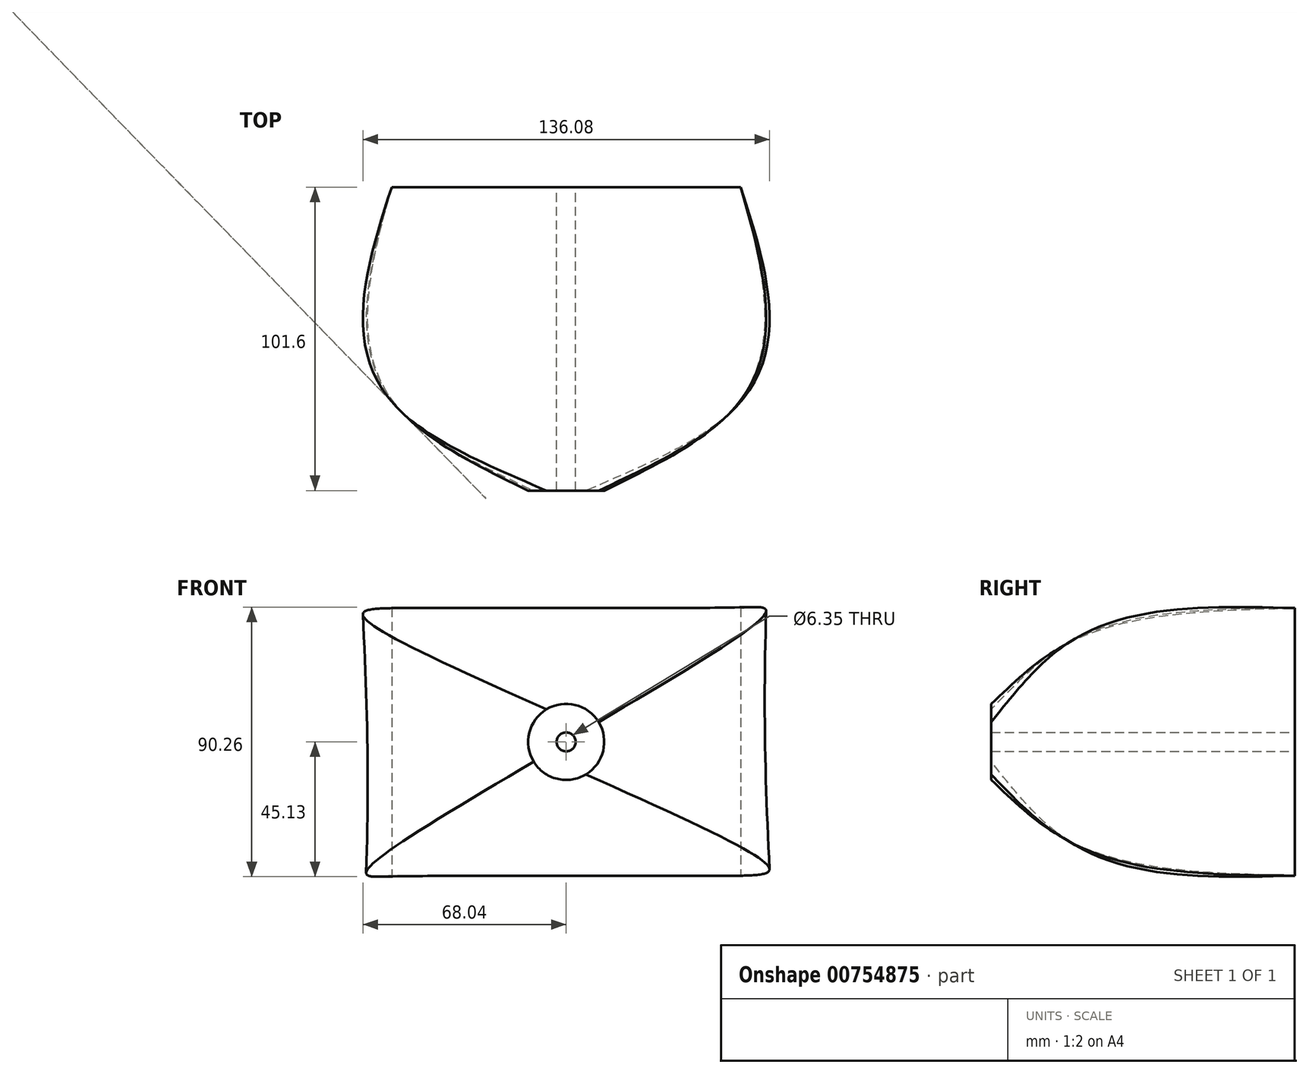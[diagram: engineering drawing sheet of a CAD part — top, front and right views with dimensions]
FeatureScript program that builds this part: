
annotation { "Feature Type Name" : "Feature", "Feature Type Description" : "" }
export const myFeature = defineFeature(function(context is Context, id is Id, definition is map)
    precondition{}
    {
        {
            var Q0;
            Q0=qCreatedBy(makeId("Front.planeOp"),FACE);
            var sketch = newSketch(context, id + "F0", { "sketchPlane" : qUnion([Q0])});
            skLineSegment(sketch, "E0.bottom", {"start": v(58.39, 44.79) * mm, "end": v(-58.39, 44.79) * mm});
            skLineSegment(sketch, "E0.top", {"start": v(58.39, -44.79) * mm, "end": v(-58.39, -44.79) * mm});
            skLineSegment(sketch, "E0.left", {"start": v(58.39, 44.79) * mm, "end": v(58.39, -44.79) * mm});
            skLineSegment(sketch, "E0.right", {"start": v(-58.39, 44.79) * mm, "end": v(-58.39, -44.79) * mm});
            skPoint(sketch, "E0.middle", {"position": v(0, 0) * mm});
            skSolve(sketch);
        }
        {
            var Q0;
            Q0=qCreatedBy(makeId("Front.planeOp"),FACE);
            cPlane(context, id + "F1", {"entities" : qUnion([Q0]), "cplaneType" : CPlaneType.OFFSET, "offset" : 76.2 * mm, "width" : 152.4 * mm, "height" : 152.4 * mm});
        }
        {
            var Q0;
            Q0=qCreatedBy(id+"F1.planeOp",FACE);
            var sketch = newSketch(context, id + "F2", { "sketchPlane" : qUnion([Q0])});
            skLineSegment(sketch, "E1.bottom", {"start": v(54.14, 32.93) * mm, "end": v(-54.14, 32.93) * mm});
            skLineSegment(sketch, "E1.top", {"start": v(54.14, -32.93) * mm, "end": v(-54.14, -32.93) * mm});
            skLineSegment(sketch, "E1.left", {"start": v(54.14, 32.93) * mm, "end": v(54.14, -32.93) * mm});
            skLineSegment(sketch, "E1.right", {"start": v(-54.14, 32.93) * mm, "end": v(-54.14, -32.93) * mm});
            skPoint(sketch, "E1.middle", {"position": v(0, 0) * mm});
            skSolve(sketch);
        }
        {
            var Q0;
            Q0=makeQuery(id+"F0.imprint","IMPRINT",FACE,{"disambiguationData":[TD([[makeQuery(id+"F0.imprint","IMPRINT",EDGE,{"derivedFrom":sQuery(id+"F0.wireOp",EDGE,"E0.bottom")}),1.0]])]});
            cPlane(context, id + "F3", {"entities" : qUnion([Q0]), "cplaneType" : CPlaneType.OFFSET, "offset" : 101.6 * mm, "width" : 152.4 * mm, "height" : 152.4 * mm});
        }
        {
            var Q0;
            Q0=qCreatedBy(id+"F3.planeOp",FACE);
            var sketch = newSketch(context, id + "F4", { "sketchPlane" : qUnion([Q0])});
            skCircle(sketch, "E2", {"center": v(0, 0) * mm, "radius": 12.73 * mm});
            skSolve(sketch);
        }
        {
            var Q0;
            Q0 = qSketchRegion(id + "F0", true);
            var Q1;
            Q1 = qSketchRegion(id + "F2", true);
            var Q2;
            Q2 = qSketchRegion(id + "F4", true);
            loft(context, id + "F5", {"sheetProfilesArray" : [{ "sheetProfileEntities" : qUnion([Q0]) }, { "sheetProfileEntities" : qUnion([Q1]) }, { "sheetProfileEntities" : qUnion([Q2]) }]});
        }
        {
            var Q0;
            Q0=makeQuery(id+"F5.opLoft","CAP_FACE",FACE,{"disambiguationData":[OSD([makeQuery(id+"F0.imprint","IMPRINT",FACE,{"disambiguationData":[TD([[makeQuery(id+"F0.imprint","IMPRINT",EDGE,{"derivedFrom":sQuery(id+"F0.wireOp",EDGE,"E0.bottom")}),1.0]])]})])],"isStart":true});
            var sketch = newSketch(context, id + "F6", { "sketchPlane" : qUnion([Q0])});
            skCircle(sketch, "E3", {"center": v(0, 0) * mm, "radius": 19.05 * mm});
            skSolve(sketch);
        }
        {
            var Q0;
            Q0=sQuery(id+"F6.wireOp",VERTEX,"E3.center");
            var Q1;
            Q1=makeQuery(id+"F5.opLoft","SWEPT_BODY",BODY,{"disambiguationData":[OSD([makeQuery(id+"F0.imprint","IMPRINT",FACE,{"disambiguationData":[TD([[makeQuery(id+"F0.imprint","IMPRINT",EDGE,{"derivedFrom":sQuery(id+"F0.wireOp",EDGE,"E0.bottom")}),1.0]])]}),sQuery(id+"F2.wireOp",EDGE,"E1.bottom"),makeQuery(id+"F4.imprint","IMPRINT",FACE,{"disambiguationData":[TD([[makeQuery(id+"F4.imprint","IMPRINT",EDGE,{"derivedFrom":sQuery(id+"F4.wireOp",EDGE,"E2")}),1.0]])]})])]});
            hole(context, id + "F7", {"style" : HoleStyle.SIMPLE, "endStyle" : HoleEndStyle.THROUGH, "holeDiameter" : 6.35 * mm, "majorDiameter" : 6.35 * mm, "isTappedThrough" : true, "tappedDepth" : 12.7 * mm, "tapClearance" : 3, "locations" : qUnion([Q0]), "scope" : qUnion([Q1])});
        }
    });
